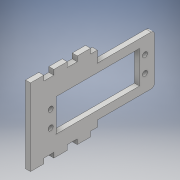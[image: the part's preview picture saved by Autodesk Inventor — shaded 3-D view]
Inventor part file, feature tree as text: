
AUTODESK INVENTOR PART (.ipt)
format: ipt  version: 2018 (Build 220112000, 112)  size: 218,112 bytes
history: native  units: mm
features: extrude x9, sketch x9, other x1, fillet x1
ambient origin geometry x8: Origin, YZ Plane, XZ Plane, XY Plane, X Axis, Y Axis, Z Axis, Center Point
bodies: Body1 (feature_tree)
feature tree (20):
  other  "Sólido1"
  extrude  "Extrusión1"  Depth=10.0mm
  extrude  "Extrusión2"  Depth=3.0mm TaperAngle=0.0deg
  extrude  "Extrusión3"  Depth=3.0mm TaperAngle=0.0deg
  extrude  "Extrusión4"  Depth=3.0mm TaperAngle=0.0deg
  extrude  "Extrusión5"  Depth=3.0mm TaperAngle=0.0deg
  extrude  "Extrusión6"  Depth=3.0mm
  extrude  "Extrusión7"  Depth=3.0mm TaperAngle=0.0deg
  extrude  "Extrusión8"  [1 undecoded]
  extrude  "Extrusión9"  [1 undecoded]
  fillet  "Empalme1"  [1 undecoded]
  sketch  "Boceto1"  dims[d1=10.0mm d2=10.0mm]
  sketch  "Boceto2"  dims[d3=10.0mm d9=3.0mm d10=0.0mm]
  sketch  "Boceto3"  dims[d11=3.0mm d12=3.0mm d13=0.0mm]
  sketch  "Boceto4"  dims[d14=10.0mm d15=0.0mm d17=3.0mm d18=0.0mm]
  sketch  "Boceto5"  dims[d31=3.0mm d32=0.0mm d39=3.0mm d40=0.0mm]
  sketch  "Boceto6"  dims[d42=3.0mm d43=0.0mm d50=4.0mm]
  sketch  "Boceto7"  dims[d51=3.0mm d52=0.0mm d55=3.0mm d56=0.0mm]
  sketch  "Boceto8"  dims[d57=2.0mm]
  sketch  "Boceto9"
note: 3 required parameter values undecoded (feature->parameter linkage not recoverable at this tier; creation-order binding heuristic only, values carry confidence <= 0.55)
